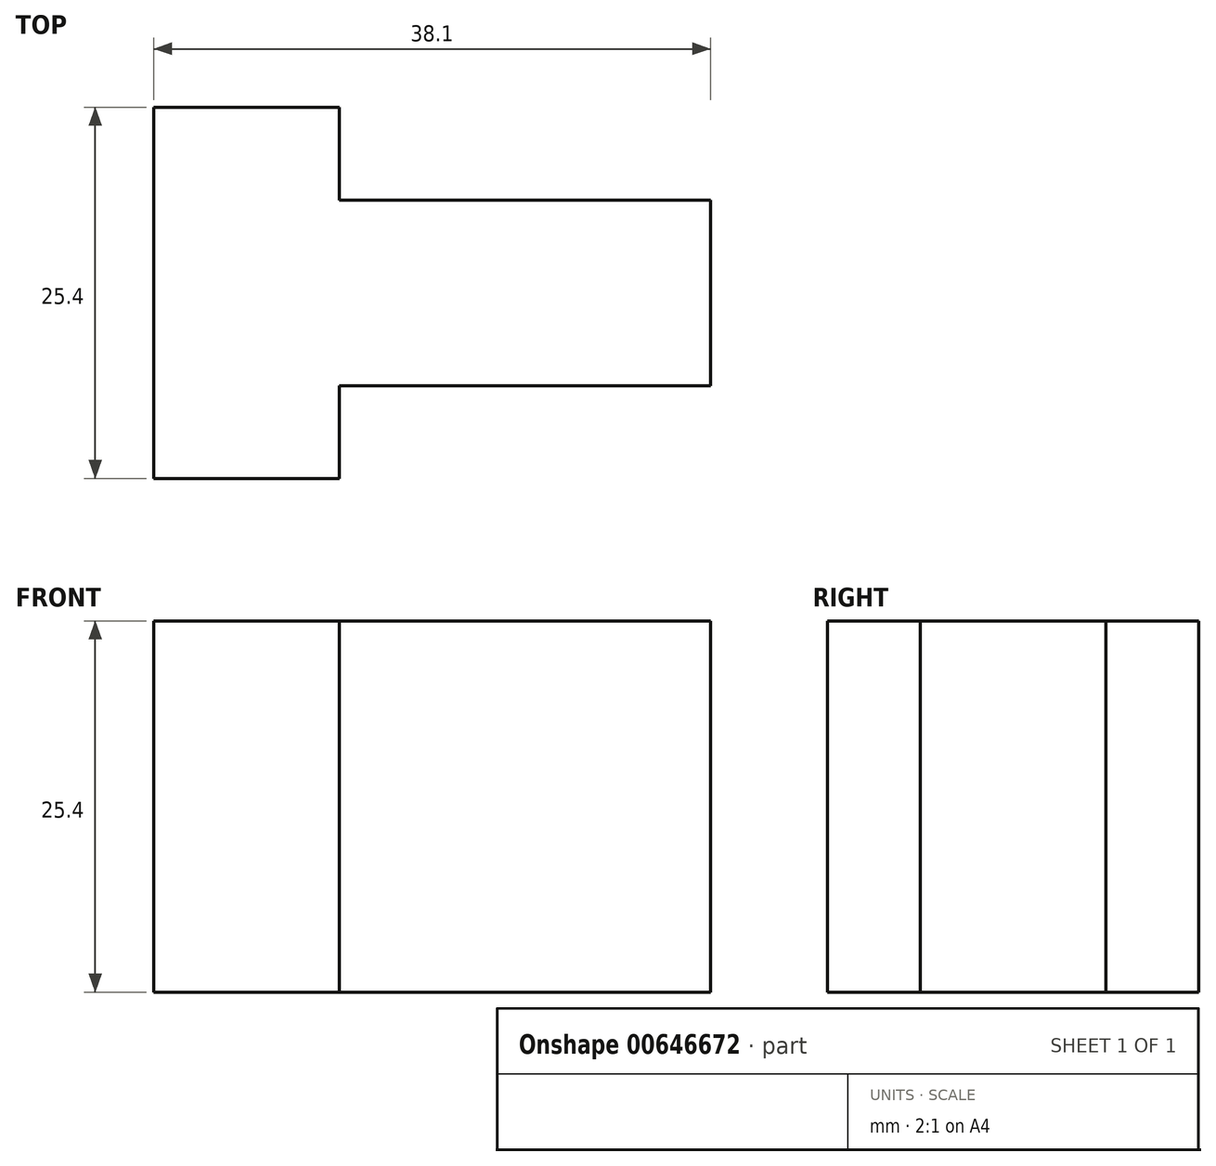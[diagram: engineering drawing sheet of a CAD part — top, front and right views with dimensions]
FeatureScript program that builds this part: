
annotation { "Feature Type Name" : "Feature", "Feature Type Description" : "" }
export const myFeature = defineFeature(function(context is Context, id is Id, definition is map)
    precondition{}
    {
        {
            var Q0;
            Q0=qCreatedBy(makeId("Top.planeOp"),FACE);
            var sketch = newSketch(context, id + "F0", { "sketchPlane" : qUnion([Q0])});
            skLineSegment(sketch, "E0", {"start": v(0, 0) * mm, "end": v(-12.7, 0) * mm});
            skLineSegment(sketch, "E1", {"start": v(-12.7, 0) * mm, "end": v(-12.7, 25.4) * mm});
            skLineSegment(sketch, "E2", {"start": v(-12.7, 25.4) * mm, "end": v(0, 25.4) * mm});
            skLineSegment(sketch, "E3", {"start": v(0, 25.4) * mm, "end": v(0, 19.05) * mm});
            skLineSegment(sketch, "E4", {"start": v(0, 19.05) * mm, "end": v(25.4, 19.05) * mm});
            skLineSegment(sketch, "E5", {"start": v(25.4, 19.05) * mm, "end": v(25.4, 6.35) * mm});
            skLineSegment(sketch, "E6", {"start": v(25.4, 6.35) * mm, "end": v(0, 6.35) * mm});
            skLineSegment(sketch, "E7", {"start": v(0, 6.35) * mm, "end": v(0, 0) * mm});
            skSolve(sketch);
        }
        {
            var Q0;
            Q0 = qSketchRegion(id + "F0", true);
            extrude(context, id + "F1", {"entities" : qUnion([Q0]), "depth" : 25.4 * mm, "offsetDistance" : 25.4 * mm});
        }
    });
